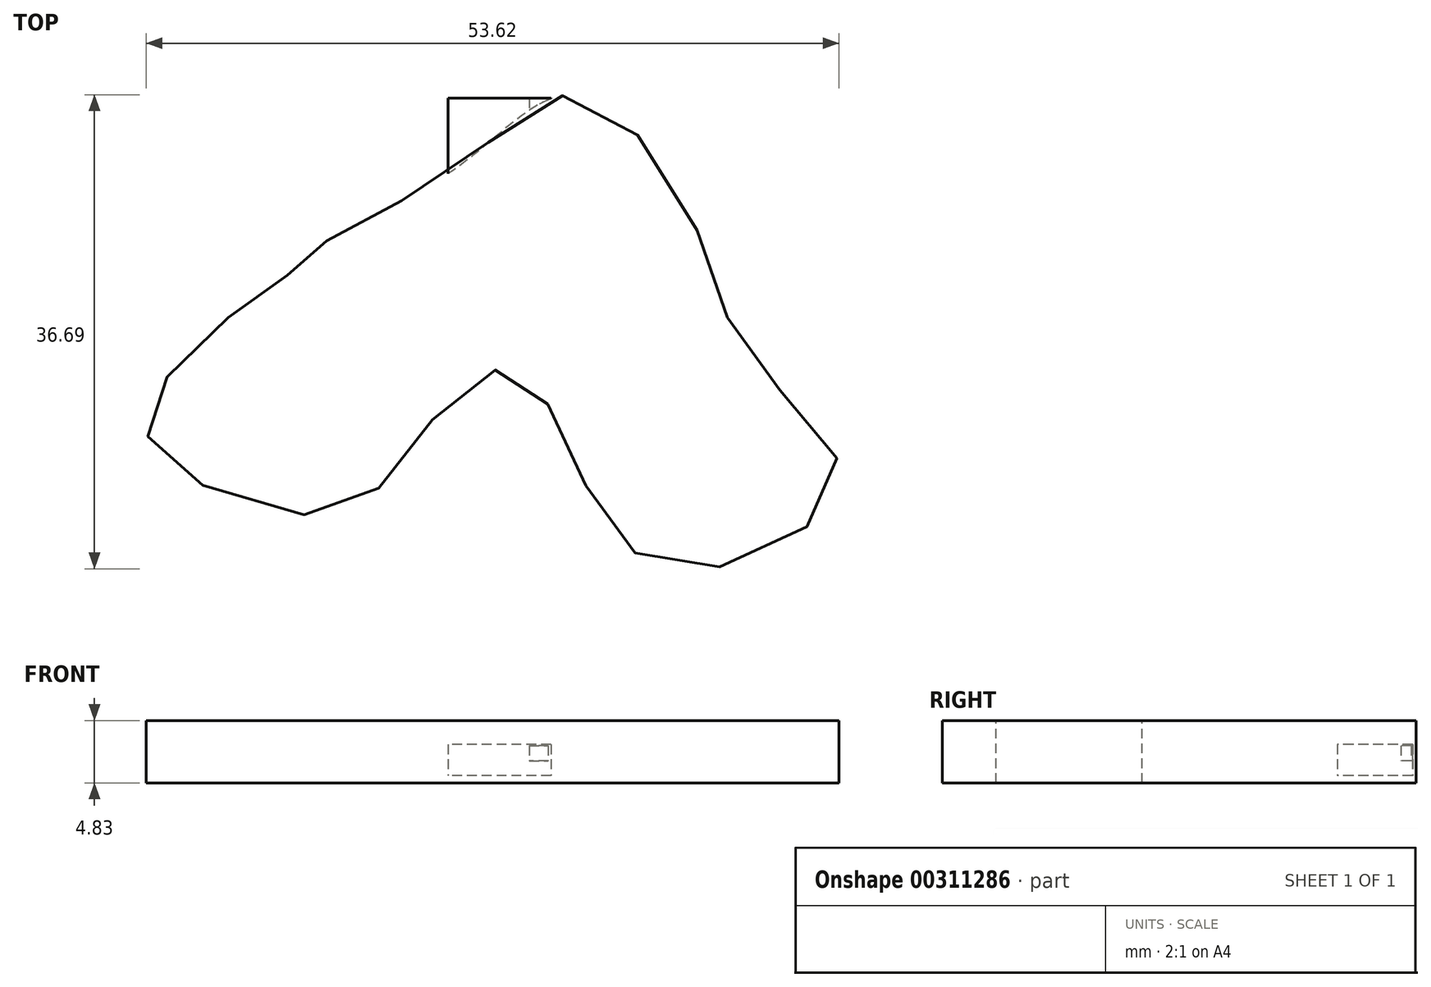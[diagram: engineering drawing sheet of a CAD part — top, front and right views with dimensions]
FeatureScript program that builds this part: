
annotation { "Feature Type Name" : "Feature", "Feature Type Description" : "" }
export const myFeature = defineFeature(function(context is Context, id is Id, definition is map)
    precondition{}
    {
        {
            var Q0;
            Q0=qCreatedBy(makeId("Top.planeOp"),FACE);
            var sketch = newSketch(context, id + "F0", { "sketchPlane" : qUnion([Q0])});
            skFitSpline(sketch, "E0", {"points": [v(-28.55, 2.45) * mm, v(-31.32, 0) * mm, v(-37.29, -4.37) * mm, v(-42.4, -10.97) * mm, v(-40.53, -15.03) * mm, v(-27.91, -18.64) * mm, v(-21.52, -12.9) * mm, v(-14.87, -7.49) * mm, v(-10.23, -12.46) * mm, v(-5.11, -21.41) * mm, v(4.97, -21.92) * mm, v(11.1, -15.06) * mm, v(4.26, -6.71) * mm, v(0, 3.52) * mm, v(-9.13, 13.7) * mm, v(-18.32, 8.2) * mm, v(-28.55, 2.45) * mm]});
            skSolve(sketch);
        }
        {
            var Q0;
            Q0=makeQuery(id+"F0.imprint","IMPRINT",FACE,{"disambiguationData":[TD([[makeQuery(id+"F0.imprint","IMPRINT",EDGE,{"derivedFrom":sQuery(id+"F0.wireOp",EDGE,"E0")}),1.0]])]});
            extrude(context, id + "F1", {"entities" : qUnion([Q0]), "depth" : 4.83 * mm});
        }
        {
            var Q0;
            Q0=qCreatedBy(makeId("Front.planeOp"),FACE);
            var sketch = newSketch(context, id + "F2", { "sketchPlane" : qUnion([Q0])});
            skLineSegment(sketch, "E1.bottom", {"start": v(-12.86, 1.7) * mm, "end": v(-11.39, 1.7) * mm});
            skLineSegment(sketch, "E1.top", {"start": v(-12.86, 2.88) * mm, "end": v(-11.39, 2.88) * mm});
            skLineSegment(sketch, "E1.left", {"start": v(-12.86, 1.7) * mm, "end": v(-12.86, 2.88) * mm});
            skLineSegment(sketch, "E1.right", {"start": v(-11.39, 1.7) * mm, "end": v(-11.39, 2.88) * mm});
            skLineSegment(sketch, "E2.bottom", {"start": v(-11.18, 2.97) * mm, "end": v(-19.13, 2.97) * mm});
            skLineSegment(sketch, "E2.top", {"start": v(-11.18, 0.55) * mm, "end": v(-19.13, 0.55) * mm});
            skLineSegment(sketch, "E2.left", {"start": v(-11.18, 2.97) * mm, "end": v(-11.18, 0.55) * mm});
            skLineSegment(sketch, "E2.right", {"start": v(-19.13, 2.97) * mm, "end": v(-19.13, 0.55) * mm});
            skSolve(sketch);
        }
        {
            var Q0;
            Q0 = qSketchRegion(id + "F2", true);
            extrude(context, id + "F3", {"entities" : qUnion([Q0]), "operationType" : NewBodyOperationType.ADD, "oppositeDirection" : true, "depth" : 13.5 * mm});
        }
    });
